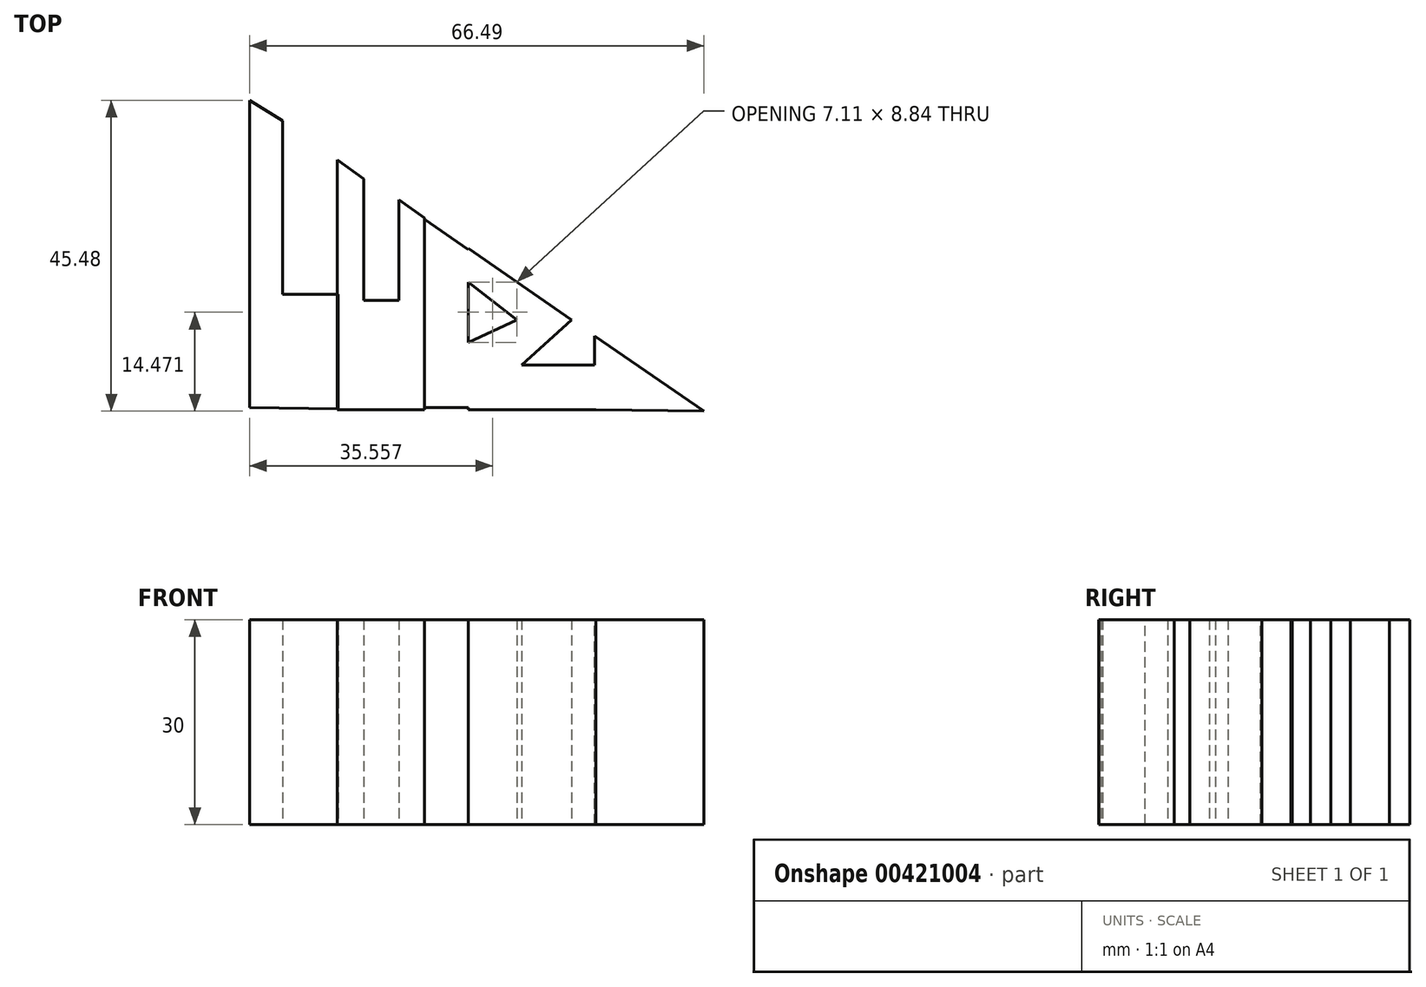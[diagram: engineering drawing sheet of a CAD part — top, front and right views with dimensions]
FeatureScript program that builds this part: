
annotation { "Feature Type Name" : "Feature", "Feature Type Description" : "" }
export const myFeature = defineFeature(function(context is Context, id is Id, definition is map)
    precondition{}
    {
        {
            var Q0;
            Q0=qCreatedBy(makeId("Top.planeOp"),FACE);
            var sketch = newSketch(context, id + "F0", { "sketchPlane" : qUnion([Q0])});
            skLineSegment(sketch, "E0", {"start": v(-25.6, 32.14) * mm, "end": v(-25.6, -12.8) * mm});
            skLineSegment(sketch, "E1", {"start": v(-12.62, -12.98) * mm, "end": v(-12.62, 3.73) * mm});
            skLineSegment(sketch, "E2", {"start": v(-12.62, 3.73) * mm, "end": v(-20.8, 3.73) * mm});
            skLineSegment(sketch, "E3", {"start": v(-20.8, 3.73) * mm, "end": v(-20.8, 29.16) * mm});
            skLineSegment(sketch, "E4", {"start": v(-20.8, 29.16) * mm, "end": v(-25.6, 32.14) * mm});
            skLineSegment(sketch, "E5", {"start": v(-25.6, -12.8) * mm, "end": v(-12.62, -12.98) * mm});
            skLineSegment(sketch, "E6", {"start": v(-12.62, -12.98) * mm, "end": v(-12.62, -12.98) * mm});
            skSolve(sketch);
        }
        {
            var Q0;
            Q0=qCreatedBy(makeId("Top.planeOp"),FACE);
            var sketch = newSketch(context, id + "F1", { "sketchPlane" : qUnion([Q0])});
            skLineSegment(sketch, "E7", {"start": v(-12.8, -13.87) * mm, "end": v(-12.8, 23.47) * mm});
            skLineSegment(sketch, "E8", {"start": v(-12.8, 23.47) * mm, "end": v(-8.9, 20.62) * mm});
            skLineSegment(sketch, "E9", {"start": v(-8.9, 20.62) * mm, "end": v(-8.9, 2.84) * mm});
            skLineSegment(sketch, "E10", {"start": v(-8.9, 2.84) * mm, "end": v(-3.73, 2.84) * mm});
            skLineSegment(sketch, "E11", {"start": v(-3.73, 2.84) * mm, "end": v(-3.73, 17.6) * mm});
            skLineSegment(sketch, "E12", {"start": v(-3.73, 17.6) * mm, "end": v(0, 14.94) * mm});
            skLineSegment(sketch, "E13", {"start": v(0, 14.94) * mm, "end": v(0, -13.16) * mm});
            skLineSegment(sketch, "E14", {"start": v(0, -13.16) * mm, "end": v(-14.94, -13.16) * mm});
            skSolve(sketch);
        }
        {
            var Q0;
            Q0=qCreatedBy(makeId("Top.planeOp"),FACE);
            var sketch = newSketch(context, id + "F2", { "sketchPlane" : qUnion([Q0])});
            skLineSegment(sketch, "E15", {"start": v(0, 14.76) * mm, "end": v(6.4, 10.31) * mm});
            skLineSegment(sketch, "E16", {"start": v(6.4, 10.31) * mm, "end": v(6.4, -12.8) * mm});
            skLineSegment(sketch, "E17", {"start": v(6.4, -12.8) * mm, "end": v(0, -12.8) * mm});
            skLineSegment(sketch, "E18", {"start": v(0, -12.8) * mm, "end": v(0, 14.76) * mm});
            skSolve(sketch);
        }
        {
            var Q0;
            Q0=qCreatedBy(makeId("Top.planeOp"),FACE);
            var sketch = newSketch(context, id + "F3", { "sketchPlane" : qUnion([Q0])});
            skLineSegment(sketch, "E19", {"start": v(6.4, 10.5) * mm, "end": v(21.51, 0) * mm});
            skLineSegment(sketch, "E20", {"start": v(21.51, 0) * mm, "end": v(14.22, -6.58) * mm});
            skLineSegment(sketch, "E21", {"start": v(14.22, -6.58) * mm, "end": v(25.07, -6.58) * mm});
            skLineSegment(sketch, "E22", {"start": v(25.07, -6.58) * mm, "end": v(25.07, -13.16) * mm});
            skLineSegment(sketch, "E23", {"start": v(25.07, -13.16) * mm, "end": v(6.4, -13.16) * mm});
            skLineSegment(sketch, "E24", {"start": v(6.4, -13.16) * mm, "end": v(6.4, -3.29) * mm});
            skPoint(sketch, "E24.endSnap0", {"position": v(17.87, -3.29) * mm});
            skLineSegment(sketch, "E25", {"start": v(6.4, -3.29) * mm, "end": v(13.51, 0) * mm});
            skLineSegment(sketch, "E26", {"start": v(13.51, 0) * mm, "end": v(6.22, 5.69) * mm});
            skLineSegment(sketch, "E27", {"start": v(6.22, 5.69) * mm, "end": v(6.4, 10.5) * mm});
            skSolve(sketch);
        }
        {
            var Q0;
            Q0=qCreatedBy(makeId("Top.planeOp"),FACE);
            var sketch = newSketch(context, id + "F4", { "sketchPlane" : qUnion([Q0])});
            skLineSegment(sketch, "E28", {"start": v(24.9, -13.16) * mm, "end": v(24.9, -2.31) * mm});
            skLineSegment(sketch, "E29", {"start": v(24.9, -2.31) * mm, "end": v(40.9, -13.34) * mm});
            skLineSegment(sketch, "E30", {"start": v(40.9, -13.34) * mm, "end": v(24.9, -13.16) * mm});
            skSolve(sketch);
        }
        {
            var Q0;
            Q0 = qSketchRegion(id + "F0", true);
            extrude(context, id + "F5", {"entities" : qUnion([Q0]), "depth" : 30 * mm});
        }
        {
            var Q0;
            Q0 = qSketchRegion(id + "F2", true);
            extrude(context, id + "F6", {"entities" : qUnion([Q0]), "depth" : 30 * mm});
        }
        {
            var Q0;
            Q0 = qSketchRegion(id + "F1", true);
            extrude(context, id + "F7", {"entities" : qUnion([Q0]), "depth" : 30 * mm});
        }
        {
            var Q0;
            Q0 = qSketchRegion(id + "F3", true);
            extrude(context, id + "F8", {"entities" : qUnion([Q0]), "operationType" : NewBodyOperationType.ADD, "depth" : 30 * mm});
        }
        {
            var Q0;
            Q0 = qSketchRegion(id + "F4", true);
            extrude(context, id + "F9", {"entities" : qUnion([Q0]), "operationType" : NewBodyOperationType.ADD, "depth" : 30 * mm});
        }
    });
